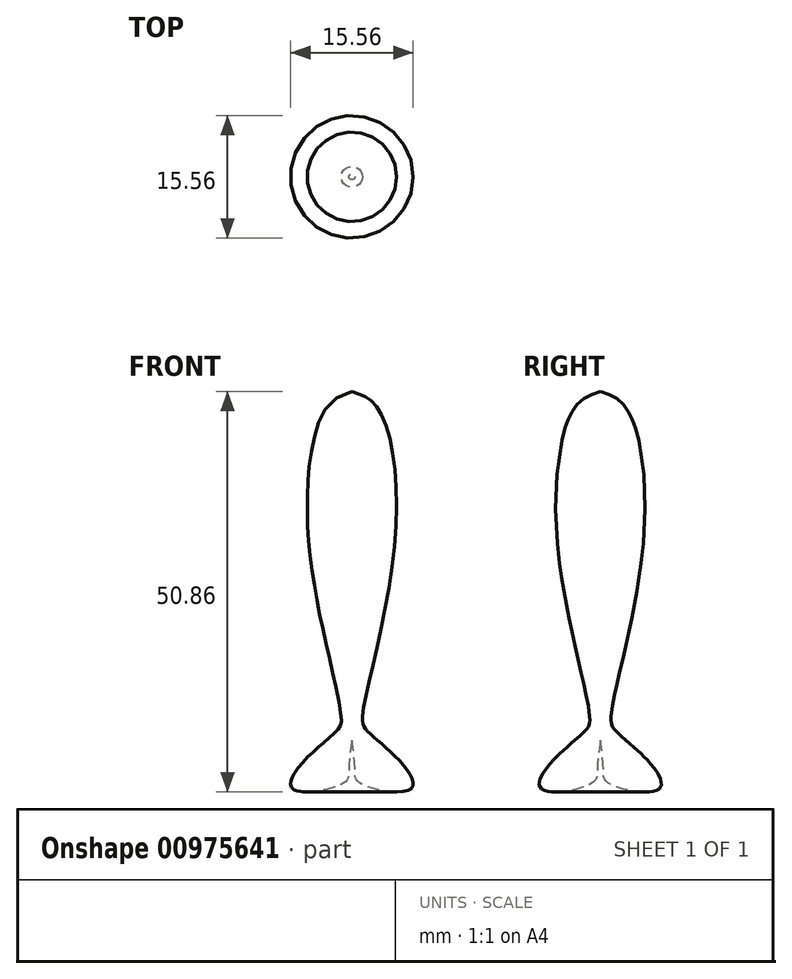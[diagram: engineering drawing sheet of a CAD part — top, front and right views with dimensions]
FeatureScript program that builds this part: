
annotation { "Feature Type Name" : "Feature", "Feature Type Description" : "" }
export const myFeature = defineFeature(function(context is Context, id is Id, definition is map)
    precondition{}
    {
        {
            var Q0;
            Q0=qCreatedBy(makeId("Front.planeOp"),FACE);
            var sketch = newSketch(context, id + "F0", { "sketchPlane" : qUnion([Q0])});
            skFitSpline(sketch, "E0", {"points": [v(0, 0) * mm, v(-3.26, -2.05) * mm, v(-5.38, -20.12) * mm, v(-1.35, -41.28) * mm, v(-1.98, -43.16) * mm, v(-6.38, -47.26) * mm, v(-7.46, -50.5) * mm, v(-0.96, -49.68) * mm, v(-0.37, -47.9) * mm, v(0, -44.34) * mm], "startDerivative": vector(-39.87, -12.63) * mm, "endDerivative": vector(6.67, 45.67) * mm});
            skLineSegment(sketch, "E1", {"start": v(0, 0) * mm, "end": v(0, -44.34) * mm});
            skFitSpline(sketch, "E2.MirrorCS", {"points": [v(0, 0) * mm, v(3.26, -2.05) * mm, v(5.38, -20.12) * mm, v(1.35, -41.28) * mm, v(1.98, -43.16) * mm, v(6.38, -47.26) * mm, v(7.46, -50.5) * mm, v(0.96, -49.68) * mm, v(0.37, -47.9) * mm, v(0, -44.34) * mm], "startDerivative": vector(39.87, -12.63) * mm, "endDerivative": vector(-6.67, 45.67) * mm});
            skLineSegment(sketch, "E3", {"start": v(-1.35, -41.28) * mm, "end": v(1.35, -41.28) * mm});
            skSolve(sketch);
        }
        {
            var Q0;
            {var subQ0=sQuery(id+"F0.wireOp",EDGE,"E2.MirrorCS");Q0=makeQuery(id+"F0.imprint","IMPRINT",FACE,{"disambiguationData":[TD([[makeQuery(id+"F0.imprint","IMPRINT",EDGE,{"derivedFrom":subQ0}),-1.0]])]});}
            var Q1;
            Q1=sQuery(id+"F0.wireOp",EDGE,"E1");
            revolve(context, id + "F1", {"surfaceOperationType" : NewSurfaceOperationType.NEW, "entities" : qUnion([Q0]), "axis" : qUnion([Q1]), "revolveType" : RevolveType.FULL});
        }
    });
